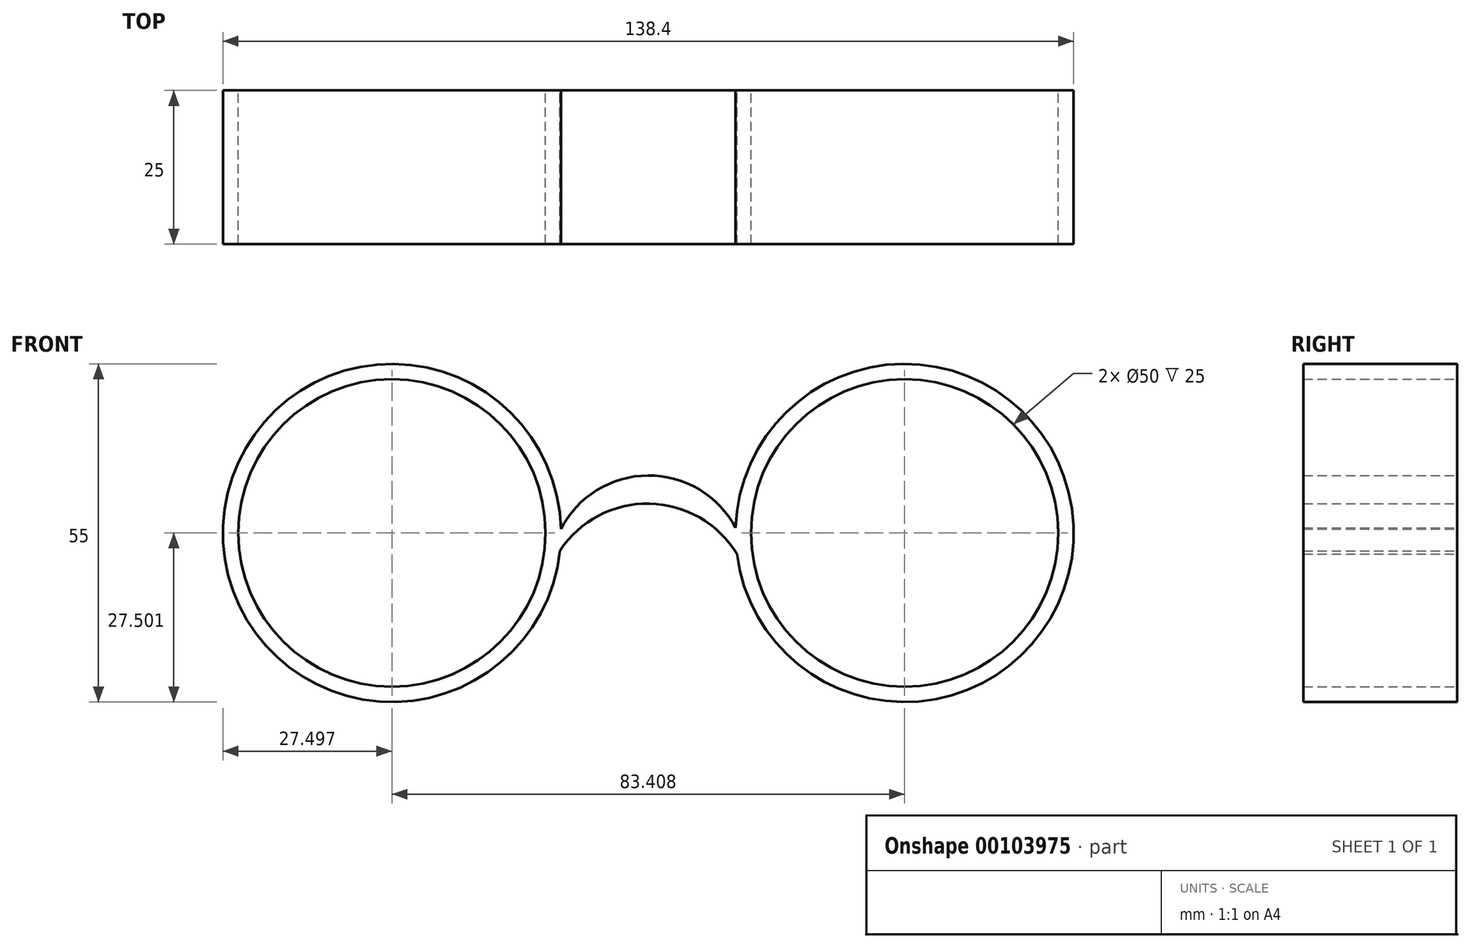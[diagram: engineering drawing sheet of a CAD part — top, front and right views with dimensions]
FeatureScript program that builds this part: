
annotation { "Feature Type Name" : "Feature", "Feature Type Description" : "" }
export const myFeature = defineFeature(function(context is Context, id is Id, definition is map)
    precondition{}
    {
        {
            var Q0;
            Q0=qCreatedBy(makeId("Front.planeOp"),FACE);
            var sketch = newSketch(context, id + "F0", { "sketchPlane" : qUnion([Q0])});
            skCircle(sketch, "E0", {"center": v(-44.35, 23.07) * mm, "radius": 25 * mm});
            skCircle(sketch, "E1", {"center": v(-44.35, 23.07) * mm, "radius": 27.5 * mm});
            skCircle(sketch, "E2", {"center": v(39.05, 23.07) * mm, "radius": 25 * mm});
            skCircle(sketch, "E3", {"center": v(39.05, 23.07) * mm, "radius": 27.5 * mm});
            skFitSpline(sketch, "E4", {"points": [v(0, 36.16) * mm, v(-6.04, 34.57) * mm], "startDerivative": vector(-6.04, -1.6) * mm, "endDerivative": vector(-6.04, -1.6) * mm});
            skArc(sketch, "E5", {"start": v(11.57, 23.9) * mm, "mid": v(-2.71, 32.42) * mm, "end": v(-16.86, 23.68) * mm});
            skArc(sketch, "E6", {"start": v(11.77, 19.65) * mm, "mid": v(-2.47, 27.85) * mm, "end": v(-17, 20.18) * mm});
            skSolve(sketch);
        }
        {
            var Q0;
            Q0 = qSketchRegion(id + "F0", true);
            extrude(context, id + "F1", {"entities" : qUnion([Q0]), "depth" : 25 * mm});
        }
    });
